# Revit family: SonoMeter40_DN50-DN100_RFA
name_source: partatom
category: Pipe Accessories
revit_build: Autodesk Revit 2017 (Build: 20161205_1400(x64)
units: mm (PartAtom-declared; Revit-internal decimal feet)

## family parameters
Always vertical = Yes
Cut with Voids When Loaded = No
Part Type = Valve - Breaks Into
Round Connector Dimension = Use Diameter
Shared = No
Work Plane-Based = No

## types (4) — shared parameters
A = 60.00°
Body Material = Danfoss Brass
Connection = Flange
Description = Energy Meter
IfcExportAs = IfcValveType
IfcExportType = SonoMeter40
L7 = 20 mm  [stored 0.0656168 ft]
L9 = 24 mm  [stored 0.0787402 ft]
LOD 200 = No
LOD 350 = Yes
Manufacturer = Danfoss
Model = SonoMeter40
Operation Pressure = PN25
URL = https://store.danfoss.com

## per-type parameters (varying)
| type | A_H1 | A_L | D | D1 | D2 | D3 | D4 | D5 | D6 | H | H1 | H2 | Kvs | L | L1 | L2 | L3 | Max Flow | Min Flow | Nominal Flow | Weight |
| SonoMeter40_DN50_Kvs43.3_270mm | 51 mm  [stored 0.167323 ft] | 17 mm | 65 mm  [stored 0.213255 ft] | 60 mm  [stored 0.19685 ft] | 70 mm | 59 mm | 160 mm  [stored 0.524934 ft] | 106 mm | 96 mm | 130 mm  [stored 0.426509 ft] | 48 mm  [stored 0.15748 ft] | 65 mm  [stored 0.213255 ft] | 43.3 m³/h | 270 mm | 264 mm | 15 mm  [stored 0.0492126 ft] | 224 mm | 30 m3/h, 50 m3/h | 0.15 m3/h, 0.35 m3/h | 15 m3/h, 25 m3/h | 8.50 kg |
| SonoMeter40_DN65_Kvs55.9_300mm | 58 mm | 22 mm  [stored 0.0721785 ft] | 65 mm  [stored 0.213255 ft] | 82 mm | 92 mm  [stored 0.301837 ft] | 75 mm | 185 mm | 131 mm | 122 mm | 165 mm  [stored 0.541339 ft] | 59 mm | 83 mm | 55.9 m³/h | 300 mm | 294 mm | 11 mm  [stored 0.0360892 ft] | 258 mm | 50 m3/h, 80 m3/h | 0.35 m3/h, 0.4 m3/h | 25 m3/h, 40 m3/h | 13.00 kg |
| SonoMeter40_DN80_Kvs94.3_300mm | 61 mm  [stored 0.200131 ft] | 23 mm  [stored 0.0754593 ft] | 80 mm  [stored 0.262467 ft] | 95 mm  [stored 0.31168 ft] | 105 mm | 80 mm  [stored 0.262467 ft] | 200 mm | 147 mm | 138 mm | 180 mm | 65 mm  [stored 0.213255 ft] | 90 mm  [stored 0.295276 ft] | 94.3 m³/h | 300 mm | 294 mm | 16 mm | 252 mm | 80 m3/h, 120 m3/h | 0.4 m3/h, 0.6 m3/h | 40 m3/h, 60 m3/h | 15.00 kg |
| SonoMeter40_DN100_Kvs141.4_360mm | 70 mm | 28 mm | 100 mm  [stored 0.328084 ft] | 115 mm  [stored 0.377297 ft] | 125 mm | 97 mm | 235 mm | 169 mm | 160 mm  [stored 0.524934 ft] | 215 mm | 73 mm | 108 mm | 141.4 m³/h | 360 mm | 354 mm | 16 mm | 312 mm | 120 m3/h | 0.6 m3/h | 60 m3/h | 18.00 kg |

note: column(s) folded — value = type name in every type: Model Type

note: [stored X ft] marks values corroborated as IEEE doubles in the binary element streams (Revit-internal decimal feet)

## geometry (parser evidence)
native form markers: Sweep x12
no freeform markers — native parametric forms only
